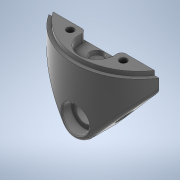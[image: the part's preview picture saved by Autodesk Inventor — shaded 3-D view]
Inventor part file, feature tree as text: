
AUTODESK INVENTOR PART (.ipt)
format: ipt  version: 2020 (Build 240168000, 168)  size: 298,496 bytes
history: native  units: in
note: dims shown in document units (in); Inventor stores cm internally (conversion verified against a paired STEP export)
features: sketch x6, extrude x3, fillet x2, revolve x1
ambient origin geometry x8: Origin, YZ Plane, XZ Plane, XY Plane, X Axis, Y Axis, Z Axis, Center Point
bodies: Solid1 (feature_tree)
feature tree (12):
  sketch  "Sketch1"  dims[d2=1.75in d3=0.125in]
  revolve  "Revolution1"  [1 undecoded]
  extrude  "Extrusion1"  Depth=0.5in
  extrude  "Extrusion3"  TaperAngle=180.0deg  [1 undecoded]
  extrude  "Extrusion7"  Depth=1.85in TaperAngle=0.0deg
  fillet  "Fillet1"  Radius=1.382in
  fillet  "Fillet2"  Radius=1.5in
  sketch  "Sketch2"  dims[d4=0.1in d5=0.5in]
  sketch  "Sketch8"  dims[d7=0.25in d9=180.0deg]
  sketch  "Sketch9"  dims[d10=1.0in d11=1.85in d12=0.0in d16=1.382in d17=0.0in d38=1.5in]
  sketch  "Sketch10"  dims[d42=1.0in]
  sketch  "Sketch11"  dims[d43=1.2in d44=0.25in d45=0.0in d46=1.2in d47=1.5in d48=0.2031in d49=0.75in d50=0.3125in d51=1.0in d52=0.5635in d53=1.0in d54=0.8108in d55=0.5in d56=0.75in d57=0.75in d58=0.3125in d59=0.5635in d60=1.0in d61=0.8108in d62=0.375in d63=0.125in d64=0.0in d65=0.0312in d66=0.125in]
note: 2 required parameter values undecoded (feature->parameter linkage not recoverable at this tier; creation-order binding heuristic only, values carry confidence <= 0.55)